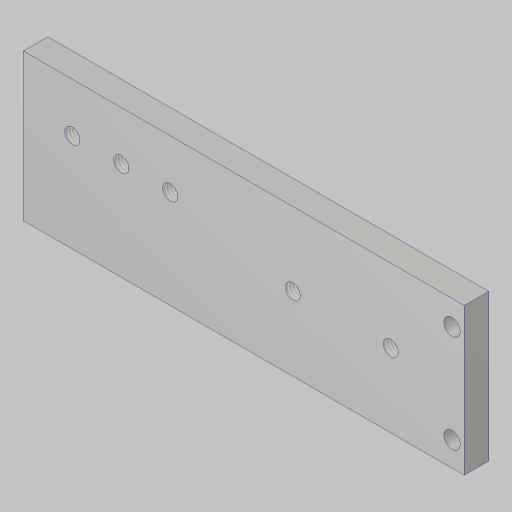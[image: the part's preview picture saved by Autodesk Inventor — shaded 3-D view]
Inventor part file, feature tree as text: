
AUTODESK INVENTOR PART (.ipt)
format: ipt  version: 2023.5 (Build 275446000, 446)  size: 130,560 bytes
history: native  units: in
note: dims shown in document units (in); Inventor stores cm internally (conversion verified against a paired STEP export)
features: sketch x4, hole x3, extrude x1
ambient origin geometry x8: Origin, YZ Plane, XZ Plane, XY Plane, X Axis, Y Axis, Z Axis, Center Point
bodies: Solid1 (feature_tree)
feature tree (8):
  extrude  "Extrusion1"  Depth=1.5in
  hole  "Hole1"  [1 undecoded]
  hole  "Hole2"  [1 undecoded]
  hole  "Hole3"  [1 undecoded]
  sketch  "Sketch1"  dims[d0=4.5in d1=1.5in]
  sketch  "Sketch2"  dims[d2=0.25in d3=0.0in d4=0.5in d5=0.5in]
  sketch  "Sketch3"  dims[d6=0.5in]
  sketch  "Sketch5"  dims[d7=0.156in d8=0.38in d9=0.385in d10=0.25in d11=0.5635in d12=1.0in d13=0.8108in d14=0.5in d15=0.5in d16=0.25in d17=0.25in d18=0.125in d19=0.17in d20=0.328in d21=0.332in d22=0.25in d23=0.5635in d24=1.0in d25=0.8108in d28=1.0in d29=0.75in d30=0.156in d31=0.38in d32=0.375in d33=0.25in d34=0.5635in d35=1.0in d36=0.8108in]
note: 3 required parameter values undecoded (feature->parameter linkage not recoverable at this tier; creation-order binding heuristic only, values carry confidence <= 0.55)
